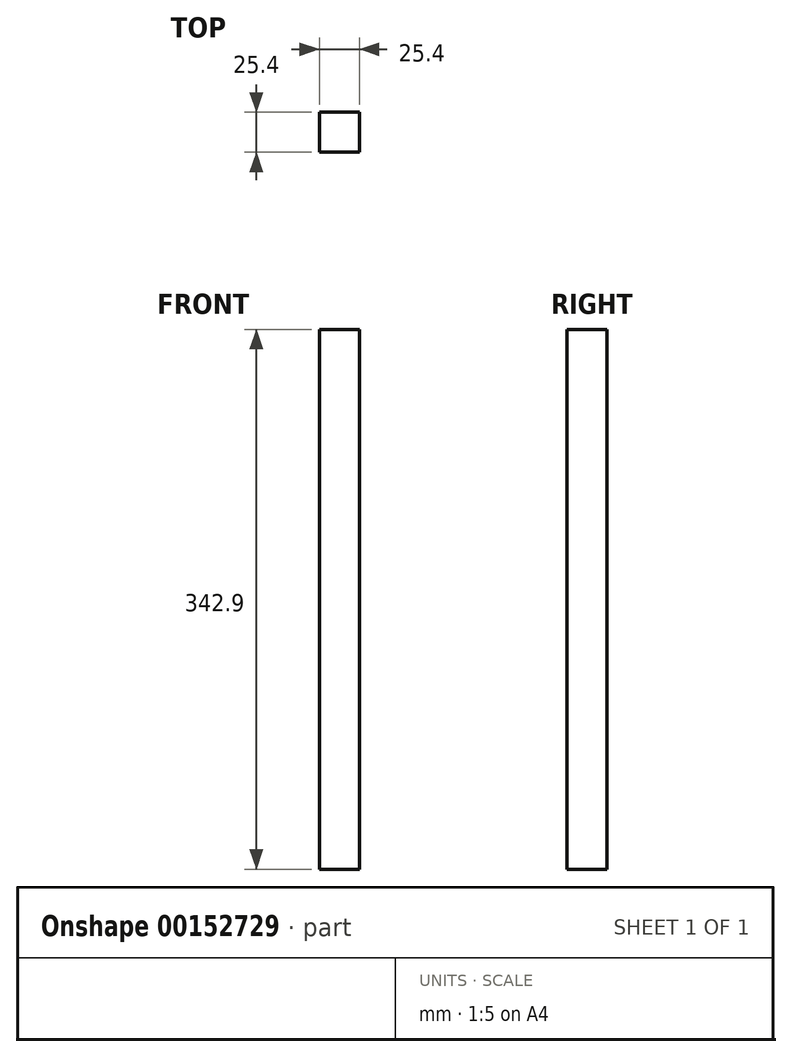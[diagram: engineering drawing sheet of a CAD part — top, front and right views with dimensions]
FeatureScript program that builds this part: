
annotation { "Feature Type Name" : "Feature", "Feature Type Description" : "" }
export const myFeature = defineFeature(function(context is Context, id is Id, definition is map)
    precondition{}
    {
        {
            var Q0;
            Q0=qCreatedBy(makeId("Top.planeOp"),FACE);
            var sketch = newSketch(context, id + "F0", { "sketchPlane" : qUnion([Q0])});
            skLineSegment(sketch, "E0.bottom", {"start": v(12.7, -12.7) * mm, "end": v(-12.7, -12.7) * mm});
            skLineSegment(sketch, "E0.top", {"start": v(12.7, 12.7) * mm, "end": v(-12.7, 12.7) * mm});
            skLineSegment(sketch, "E0.left", {"start": v(12.7, -12.7) * mm, "end": v(12.7, 12.7) * mm});
            skLineSegment(sketch, "E0.right", {"start": v(-12.7, -12.7) * mm, "end": v(-12.7, 12.7) * mm});
            skPoint(sketch, "E0.middle", {"position": v(0, 0) * mm});
            skSolve(sketch);
        }
        {
            var Q0;
            Q0 = qSketchRegion(id + "F0", true);
            extrude(context, id + "F1", {"entities" : qUnion([Q0]), "depth" : 342.9 * mm});
        }
    });
